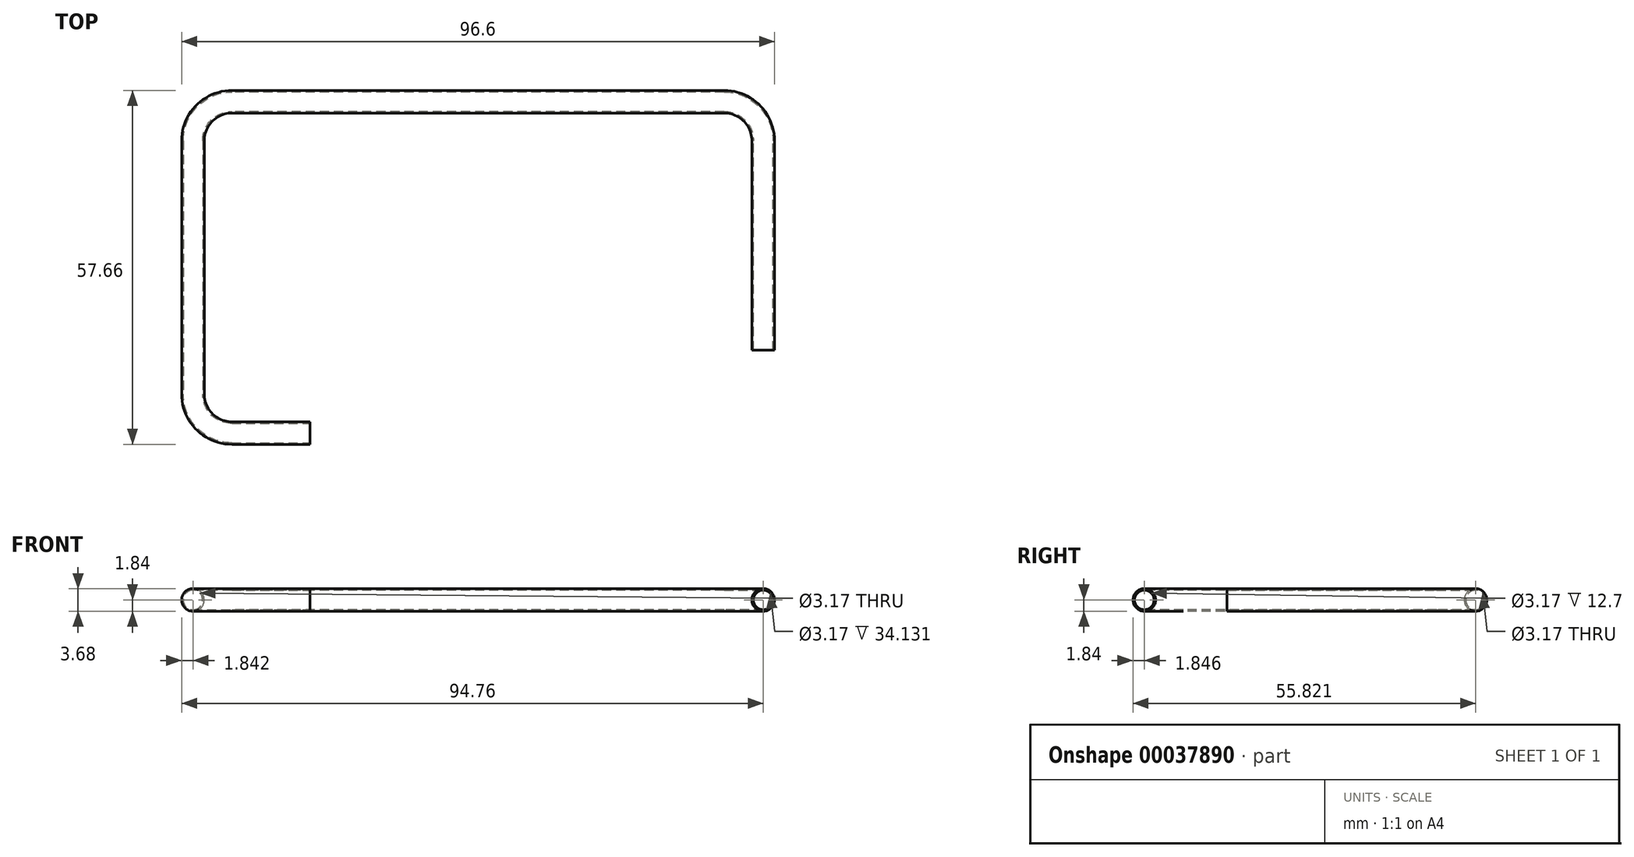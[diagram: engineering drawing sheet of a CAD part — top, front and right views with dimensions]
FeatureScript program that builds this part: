
annotation { "Feature Type Name" : "Feature", "Feature Type Description" : "" }
export const myFeature = defineFeature(function(context is Context, id is Id, definition is map)
    precondition{}
    {
        {
            var Q0;
            Q0=qCreatedBy(makeId("Top.planeOp"),FACE);
            var sketch = newSketch(context, id + "F0", { "sketchPlane" : qUnion([Q0])});
            skLineSegment(sketch, "E0", {"start": v(-73.87, -13.5) * mm, "end": v(-9.15, -13.5) * mm, "construction": true});
            skLineSegment(sketch, "E1", {"start": v(0, 0) * mm, "end": v(0, 34.13) * mm});
            skLineSegment(sketch, "E2", {"start": v(-9.15, -13.5) * mm, "end": v(-9.15, 0) * mm, "construction": true});
            skArc(sketch, "E3", {"start": v(0, 34.13) * mm, "mid": v(-1.86, 38.62) * mm, "end": v(-6.35, 40.48) * mm});
            skLineSegment(sketch, "E4", {"start": v(-86.57, 40.48) * mm, "end": v(-6.35, 40.48) * mm});
            skArc(sketch, "E5", {"start": v(-92.92, -7.14) * mm, "mid": v(-91.06, -11.63) * mm, "end": v(-86.57, -13.5) * mm});
            skLineSegment(sketch, "E6", {"start": v(-92.92, -7.14) * mm, "end": v(-92.92, 34.13) * mm});
            skLineSegment(sketch, "E7.top", {"start": v(-9.15, 0) * mm, "end": v(0, 0) * mm, "construction": true});
            skLineSegment(sketch, "E7.left", {"start": v(-9.15, 11.9) * mm, "end": v(-9.15, 0) * mm, "construction": true});
            skArc(sketch, "E8", {"start": v(-86.57, 40.48) * mm, "mid": v(-91.06, 38.62) * mm, "end": v(-92.92, 34.13) * mm});
            skLineSegment(sketch, "E9", {"start": v(-73.87, -13.5) * mm, "end": v(-86.57, -13.5) * mm});
            skSolve(sketch);
        }
        {
            var Q0;
            Q0=qCreatedBy(makeId("Front.planeOp"),FACE);
            var sketch = newSketch(context, id + "F1", { "sketchPlane" : qUnion([Q0])});
            skCircle(sketch, "E10", {"center": v(0, 0) * mm, "radius": 1.59 * mm});
            skCircle(sketch, "E11", {"center": v(0, 0) * mm, "radius": 1.84 * mm});
            skSolve(sketch);
        }
        {
            var Q0;
            Q0=makeQuery(id+"F1.imprint","IMPRINT",FACE,{"disambiguationData":[TD([[makeQuery(id+"F1.imprint","IMPRINT",EDGE,{"derivedFrom":sQuery(id+"F1.wireOp",EDGE,"E10")}),-1.0]])]});
            var Q1;
            Q1=sQuery(id+"F0.wireOp",EDGE,"E1");
            var Q2;
            Q2=sQuery(id+"F0.wireOp",EDGE,"E3");
            var Q3;
            Q3=sQuery(id+"F0.wireOp",EDGE,"E4");
            var Q4;
            Q4=sQuery(id+"F0.wireOp",EDGE,"E8");
            var Q5;
            Q5=sQuery(id+"F0.wireOp",EDGE,"E6");
            var Q6;
            Q6=sQuery(id+"F0.wireOp",EDGE,"E5");
            var Q7;
            Q7=sQuery(id+"F0.wireOp",EDGE,"E9");
            sweep(context, id + "F2", {"profiles" : qUnion([Q0]), "path" : qUnion([Q1, Q2, Q3, Q4, Q5, Q6, Q7])});
        }
    });
